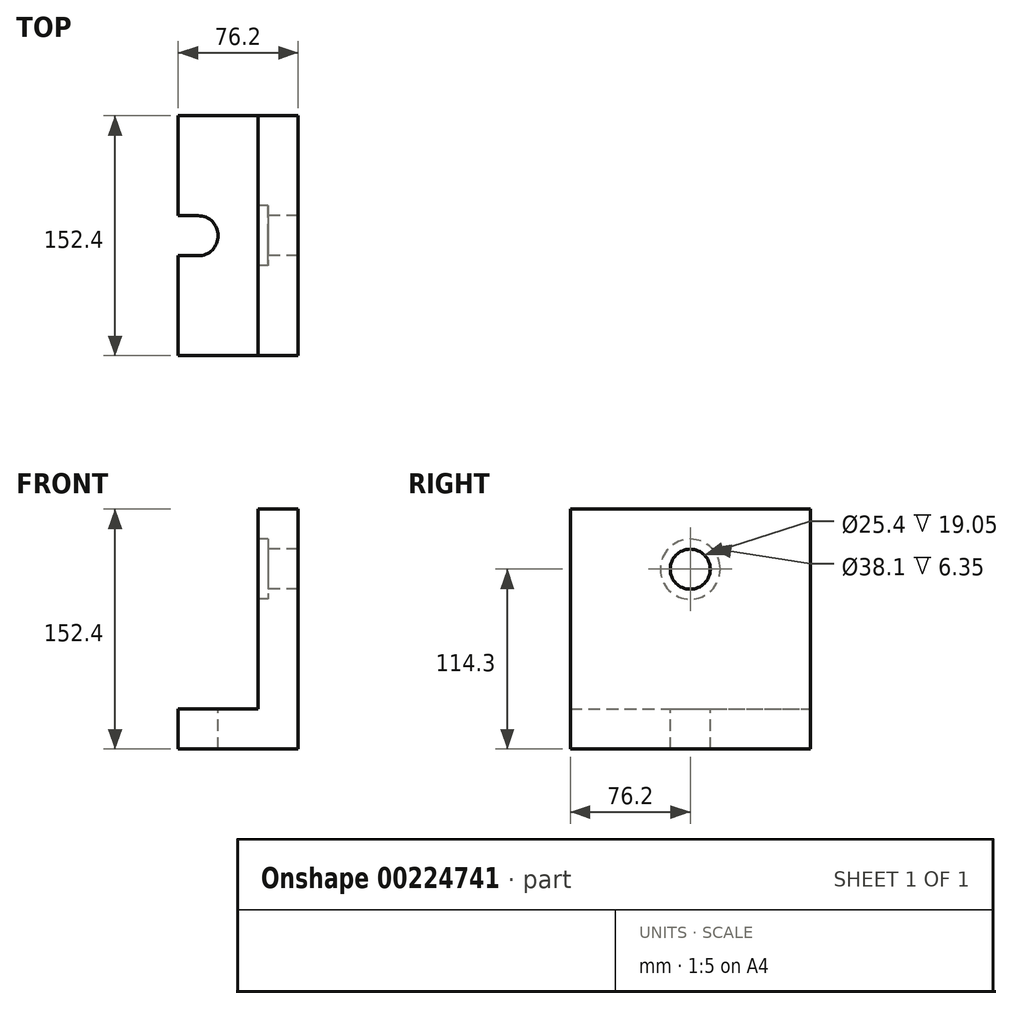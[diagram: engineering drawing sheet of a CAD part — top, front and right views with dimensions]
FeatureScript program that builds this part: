
annotation { "Feature Type Name" : "Feature", "Feature Type Description" : "" }
export const myFeature = defineFeature(function(context is Context, id is Id, definition is map)
    precondition{}
    {
        {
            var Q0;
            Q0=qCreatedBy(makeId("Front.planeOp"),FACE);
            var sketch = newSketch(context, id + "F0", { "sketchPlane" : qUnion([Q0])});
            skLineSegment(sketch, "E0", {"start": v(0, 0) * mm, "end": v(0, 152.4) * mm});
            skLineSegment(sketch, "E1", {"start": v(0, 152.4) * mm, "end": v(-25.4, 152.4) * mm});
            skLineSegment(sketch, "E2", {"start": v(-25.4, 152.4) * mm, "end": v(-25.4, 25.4) * mm});
            skLineSegment(sketch, "E3", {"start": v(-25.4, 25.4) * mm, "end": v(-76.2, 25.4) * mm});
            skLineSegment(sketch, "E4", {"start": v(-76.2, 25.4) * mm, "end": v(-76.2, 0) * mm});
            skLineSegment(sketch, "E5", {"start": v(-76.2, 0) * mm, "end": v(0, 0) * mm});
            skSolve(sketch);
        }
        {
            var Q0;
            Q0 = qSketchRegion(id + "F0", true);
            extrude(context, id + "F1", {"entities" : qUnion([Q0]), "endBound" : BoundingType.SYMMETRIC, "depth" : 152.4 * mm});
        }
        {
            var Q0;
            Q0=makeQuery(id+"F1.opExtrude","SWEPT_FACE",FACE,{"disambiguationData":[OSD([sQuery(id+"F0.wireOp",EDGE,"E2")])]});
            var sketch = newSketch(context, id + "F2", { "sketchPlane" : qUnion([Q0])});
            skCircle(sketch, "E6", {"center": v(0, 114.3) * mm, "radius": 12.7 * mm});
            skCircle(sketch, "E7", {"center": v(0, 114.3) * mm, "radius": 19.05 * mm});
            skSolve(sketch);
        }
        {
            var Q0;
            Q0=makeQuery(id+"F2.imprint","IMPRINT",FACE,{"disambiguationData":[TD([[makeQuery(id+"F2.imprint","IMPRINT",EDGE,{"derivedFrom":sQuery(id+"F2.wireOp",EDGE,"E6")}),1.0]])]});
            extrude(context, id + "F3", {"entities" : qUnion([Q0]), "operationType" : NewBodyOperationType.REMOVE, "endBound" : BoundingType.THROUGH_ALL, "oppositeDirection" : true, "depth" : 25.4 * mm});
        }
        {
            var Q0;
            Q0=makeQuery(id+"F2.imprint","IMPRINT",FACE,{"disambiguationData":[TD([[makeQuery(id+"F2.imprint","IMPRINT",EDGE,{"derivedFrom":sQuery(id+"F2.wireOp",EDGE,"E6")}),-1.0]])]});
            extrude(context, id + "F4", {"entities" : qUnion([Q0]), "operationType" : NewBodyOperationType.REMOVE, "oppositeDirection" : true, "depth" : 6.35 * mm});
        }
        {
            var Q0;
            Q0=makeQuery(id+"F1.opExtrude","SWEPT_FACE",FACE,{"disambiguationData":[OSD([sQuery(id+"F0.wireOp",EDGE,"E3")])]});
            var sketch = newSketch(context, id + "F5", { "sketchPlane" : qUnion([Q0])});
            skLineSegment(sketch, "E8", {"start": v(-76.2, 0) * mm, "end": v(-76.2, 12.7) * mm});
            skLineSegment(sketch, "E9", {"start": v(-76.2, 12.7) * mm, "end": v(-63.5, 12.7) * mm});
            skLineSegment(sketch, "E10", {"start": v(-76.2, 0) * mm, "end": v(-76.2, -12.7) * mm});
            skLineSegment(sketch, "E11", {"start": v(-76.2, -12.7) * mm, "end": v(-63.5, -12.7) * mm});
            skArc(sketch, "E12", {"start": v(-63.5, -12.7) * mm, "mid": v(-50.8, 0) * mm, "end": v(-63.5, 12.7) * mm});
            skSolve(sketch);
        }
        {
            var Q0;
            Q0 = qSketchRegion(id + "F5", true);
            extrude(context, id + "F6", {"entities" : qUnion([Q0]), "operationType" : NewBodyOperationType.REMOVE, "endBound" : BoundingType.THROUGH_ALL, "oppositeDirection" : true, "depth" : 25.4 * mm});
        }
    });
